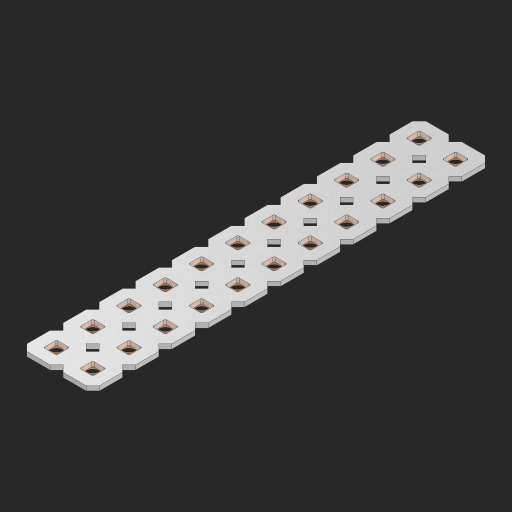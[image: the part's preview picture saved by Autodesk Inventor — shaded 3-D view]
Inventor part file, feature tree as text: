
AUTODESK INVENTOR PART (.ipt)
format: ipt  version: 2023 (Build 270158000, 158)  size: 529,408 bytes
history: native  units: in
note: dims shown in document units (in); Inventor stores cm internally (conversion verified against a paired STEP export)
features: other x23, extrude x21, sketch x2, pattern_linear x1
ambient origin geometry x8: Origin, YZ Plane, XZ Plane, XY Plane, X Axis, Y Axis, Z Axis, Center Point
bodies: Solid1 (feature_tree), Body (feature_tree)
feature tree (47):
  pattern_linear  "Rectangular Pattern1"  Spacing1=0.09in  [1 undecoded]
  sketch  "Sketch1"  dims[d1=0.5in]
  sketch  "Sketch2"  dims[d2=0.182in d3=0.09in d4=0.09in d5=0.09in d6=0.09in d7=0.09in d8=0.09in d9=0.09in d10=0.09in d11=0.02in d13=0.0in d14=0.172in d15=0.0625in d16=0.0in d19=0.5in d22=0.5in]
  other  "Srf1"
  other  "Srf126"
  other  "Srf127"
  other  "Srf128"
  other  "Srf129"
  other  "Srf130"
  other  "Srf131"
  other  "Srf250"
  other  "Srf251"
  other  "Srf252"
  other  "Srf253"
  other  "Srf268"
  other  "Srf269"
  other  "Srf270"
  other  "Srf271"
  other  "Srf272"
  other  "Srf273"
  other  "Srf274"
  other  "Srf275"
  other  "Srf276"
  other  "Srf277"
  other  "Srf278"
  other  "Circle"
  extrude  "ExtrusionSrf126"  Depth=0.09in
  extrude  "ExtrusionSrf127"  Depth=0.09in
  extrude  "ExtrusionSrf128"  Depth=0.09in
  extrude  "ExtrusionSrf129"  Depth=0.09in
  extrude  "ExtrusionSrf130"  Depth=0.09in
  extrude  "ExtrusionSrf131"  Depth=0.09in
  extrude  "ExtrusionSrf250"  Depth=0.09in
  extrude  "ExtrusionSrf251"  Depth=0.02in
  extrude  "ExtrusionSrf252"  TaperAngle=0.0deg  [1 undecoded]
  extrude  "ExtrusionSrf253"  Depth=0.5in
  extrude  "ExtrusionSrf268"  Depth=0.0625in TaperAngle=0.0deg
  extrude  "ExtrusionSrf269"  Depth=0.5in
  extrude  "ExtrusionSrf270"  Depth=0.5in
  extrude  "ExtrusionSrf271"  [1 undecoded]
  extrude  "ExtrusionSrf272"  [1 undecoded]
  extrude  "ExtrusionSrf273"  [1 undecoded]
  extrude  "ExtrusionSrf274"  [1 undecoded]
  extrude  "ExtrusionSrf275"  [1 undecoded]
  extrude  "ExtrusionSrf276"  [1 undecoded]
  extrude  "ExtrusionSrf277"  [1 undecoded]
  extrude  "ExtrusionSrf278"  [1 undecoded]
note: 10 required parameter values undecoded (feature->parameter linkage not recoverable at this tier; creation-order binding heuristic only, values carry confidence <= 0.55)
